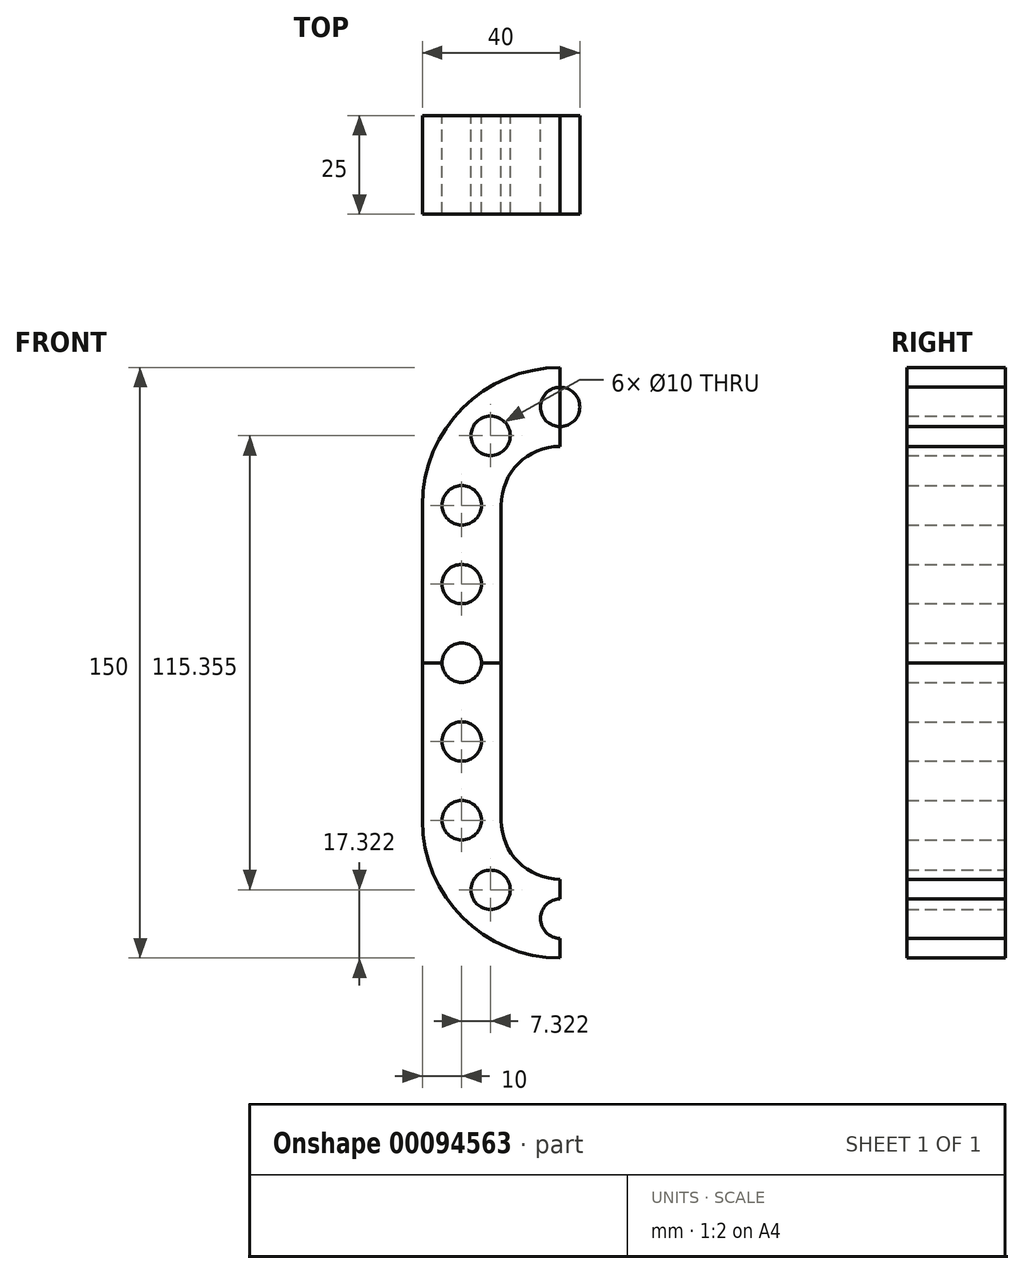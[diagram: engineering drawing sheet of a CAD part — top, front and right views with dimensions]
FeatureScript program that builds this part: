
annotation { "Feature Type Name" : "Feature", "Feature Type Description" : "" }
export const myFeature = defineFeature(function(context is Context, id is Id, definition is map)
    precondition{}
    {
        {
            var Q0;
            Q0=qCreatedBy(makeId("Front.planeOp"),FACE);
            var sketch = newSketch(context, id + "F0", { "sketchPlane" : qUnion([Q0])});
            skPoint(sketch, "E0", {"position": v(-25, 40) * mm});
            skLineSegment(sketch, "E1", {"start": v(-25, 40) * mm, "end": v(-25, 0) * mm, "construction": true});
            skArc(sketch, "E2", {"start": v(0, 65) * mm, "mid": v(-17.68, 57.68) * mm, "end": v(-25, 40) * mm, "construction": true});
            skLineSegment(sketch, "E3.0", {"start": v(-35, 40) * mm, "end": v(-35, 0) * mm});
            skArc(sketch, "E3.1", {"start": v(0, 75) * mm, "mid": v(-24.75, 64.75) * mm, "end": v(-35, 40) * mm});
            skLineSegment(sketch, "E4.0", {"start": v(-15, 40) * mm, "end": v(-15, 0) * mm});
            skArc(sketch, "E4.1", {"start": v(0, 55) * mm, "mid": v(-10.6, 50.6) * mm, "end": v(-15, 40) * mm});
            skArc(sketch, "E5.0.left", {"start": v(0, 55) * mm, "mid": v(-10.6, 50.6) * mm, "end": v(-15, 40) * mm, "construction": true});
            skArc(sketch, "E5.0.right", {"start": v(0, 75) * mm, "mid": v(-24.75, 64.75) * mm, "end": v(-35, 40) * mm, "construction": true});
            skLineSegment(sketch, "E5.1.startCap", {"start": v(-15, 40) * mm, "end": v(-15, 40) * mm});
            skLineSegment(sketch, "E5.1.left", {"start": v(-15, 40) * mm, "end": v(-15, 0) * mm, "construction": true});
            skLineSegment(sketch, "E5.1.right", {"start": v(-15, 40) * mm, "end": v(-15, 0) * mm, "construction": true});
            skCircle(sketch, "E6", {"center": v(-25, 40) * mm, "radius": 5 * mm});
            skArc(sketch, "E7.0.1.0", {"start": v(-25, 25) * mm, "mid": v(-30, 20) * mm, "end": v(-25, 15) * mm});
            skArc(sketch, "E7.0.2.0", {"start": v(-20, 0) * mm, "mid": v(-25, 5) * mm, "end": v(-30, 0) * mm});
            skLineSegment(sketch, "E7.direction1", {"start": v(-25, 40) * mm, "end": v(0, 40) * mm, "construction": true});
            skLineSegment(sketch, "E7.direction2", {"start": v(-25, 40) * mm, "end": v(-25, 20) * mm, "construction": true});
            skCircle(sketch, "E8.1.0", {"center": v(-17.68, 57.68) * mm, "radius": 5 * mm});
            skArc(sketch, "E8.2.0", {"start": v(0, 70) * mm, "mid": v(-5, 65) * mm, "end": v(0, 60) * mm});
            skLineSegment(sketch, "E8.anchor1", {"start": v(0, 40) * mm, "end": v(-25, 40) * mm, "construction": true});
            skLineSegment(sketch, "E8.anchor2", {"start": v(0, 40) * mm, "end": v(0, 65) * mm, "construction": true});
            skLineSegment(sketch, "E9", {"start": v(-15, 0) * mm, "end": v(-35, 0) * mm});
            skLineSegment(sketch, "E10", {"start": v(0, 75) * mm, "end": v(0, 55) * mm});
            skArc(sketch, "E11.MirrorCS", {"start": v(-25, 25) * mm, "mid": v(-20, 20) * mm, "end": v(-25, 15) * mm});
            skLineSegment(sketch, "E12.MirrorCS", {"start": v(15, 40) * mm, "end": v(15, 0) * mm, "construction": true});
            skArc(sketch, "E13.MirrorCS", {"start": v(0, 75) * mm, "mid": v(24.75, 64.75) * mm, "end": v(35, 40) * mm, "construction": true});
            skArc(sketch, "E14.MirrorCS", {"start": v(0, 55) * mm, "mid": v(10.6, 50.6) * mm, "end": v(15, 40) * mm, "construction": true});
            skLineSegment(sketch, "E15.MirrorCS", {"start": v(25, 40) * mm, "end": v(25, 20) * mm, "construction": true});
            skLineSegment(sketch, "E16.MirrorCS", {"start": v(25, 40) * mm, "end": v(0, 40) * mm, "construction": true});
            skArc(sketch, "E17.MirrorCS", {"start": v(25, 25) * mm, "mid": v(30, 20) * mm, "end": v(25, 15) * mm});
            skCircle(sketch, "E18.MirrorC", {"center": v(25, 40) * mm, "radius": 5 * mm});
            skArc(sketch, "E19.MirrorCS", {"start": v(0, 55) * mm, "mid": v(10.6, 50.6) * mm, "end": v(15, 40) * mm});
            skLineSegment(sketch, "E20.MirrorCS", {"start": v(15, 40) * mm, "end": v(15, 0) * mm});
            skArc(sketch, "E21.MirrorCS", {"start": v(0, 75) * mm, "mid": v(24.75, 64.75) * mm, "end": v(35, 40) * mm});
            skLineSegment(sketch, "E22.MirrorCS", {"start": v(35, 40) * mm, "end": v(35, 0) * mm});
            skLineSegment(sketch, "E23.MirrorCS", {"start": v(0, 40) * mm, "end": v(25, 40) * mm, "construction": true});
            skLineSegment(sketch, "E24.MirrorCS", {"start": v(25, 40) * mm, "end": v(25, 0) * mm, "construction": true});
            skCircle(sketch, "E25.MirrorC", {"center": v(17.68, 57.68) * mm, "radius": 5 * mm});
            skArc(sketch, "E26.MirrorCS", {"start": v(20, 0) * mm, "mid": v(25, 5) * mm, "end": v(30, 0) * mm});
            skArc(sketch, "E27.MirrorCS", {"start": v(25, 25) * mm, "mid": v(20, 20) * mm, "end": v(25, 15) * mm});
            skArc(sketch, "E28.MirrorCS", {"start": v(0, 70) * mm, "mid": v(5, 65) * mm, "end": v(0, 60) * mm});
            skLineSegment(sketch, "E29.MirrorCS", {"start": v(15, 0) * mm, "end": v(35, 0) * mm});
            skLineSegment(sketch, "E30.MirrorCS", {"start": v(15, 40) * mm, "end": v(15, 40) * mm});
            skArc(sketch, "E31.MirrorCS", {"start": v(0, 65) * mm, "mid": v(17.68, 57.68) * mm, "end": v(25, 40) * mm, "construction": true});
            skSolve(sketch);
        }
        {
            var Q0;
            {var subQ0=sQuery(id+"F0.wireOp",EDGE,"E3.0");Q0=makeQuery(id+"F0.imprint","IMPRINT",FACE,{"disambiguationData":[TD([[makeQuery(id+"F0.imprint","IMPRINT",EDGE,{"derivedFrom":subQ0}),1.0]])]});}
            var Q1;
            {var subQ0=sQuery(id+"F0.wireOp",EDGE,"E3.0");Q1=makeQuery(id+"F0.imprint","IMPRINT",FACE,{"disambiguationData":[TD([[makeQuery(id+"F0.imprint","IMPRINT",EDGE,{"derivedFrom":subQ0}),1.0]])]});}
            var Q2;
            Q2=makeQuery(id+"F0.imprint","IMPRINT",FACE,{"disambiguationData":[TD([[makeQuery(id+"F0.imprint","IMPRINT",EDGE,{"derivedFrom":sQuery(id+"F0.wireOp",EDGE,"E8.1.0")}),-1.0]])]});
            var Q3;
            {var subQ5=sQuery(id+"F0.wireOp",EDGE,"E28.MirrorCS");Q3=makeQuery(id+"F0.imprint","IMPRINT",FACE,{"disambiguationData":[TD([[makeQuery(id+"F0.imprint","IMPRINT",EDGE,{"derivedFrom":subQ5}),1.0]])]});}
            extrude(context, id + "F1", {"entities" : qUnion([Q0, Q1, Q2, Q3]), "depth" : 25 * mm});
        }
        {
            var Q0;
            Q0=makeQuery(id+"F1.opExtrude","SWEPT_BODY",BODY,{"disambiguationData":[OSD([sQuery(id+"F0.wireOp",EDGE,"E9"),sQuery(id+"F0.wireOp",EDGE,"E29.MirrorCS"),sQuery(id+"F0.wireOp",EDGE,"E28.MirrorCS"),sQuery(id+"F0.wireOp",EDGE,"E8.1.0"),sQuery(id+"F0.wireOp",EDGE,"E6"),sQuery(id+"F0.wireOp",EDGE,"E21.MirrorCS"),sQuery(id+"F0.wireOp",EDGE,"E7.0.1.0"),sQuery(id+"F0.wireOp",EDGE,"E20.MirrorCS"),sQuery(id+"F0.wireOp",EDGE,"E19.MirrorCS"),sQuery(id+"F0.wireOp",EDGE,"E18.MirrorC"),sQuery(id+"F0.wireOp",EDGE,"E17.MirrorCS"),sQuery(id+"F0.wireOp",EDGE,"E26.MirrorCS"),sQuery(id+"F0.wireOp",EDGE,"E3.1"),sQuery(id+"F0.wireOp",EDGE,"E8.2.0"),sQuery(id+"F0.wireOp",EDGE,"E4.0"),sQuery(id+"F0.wireOp",EDGE,"E4.1"),sQuery(id+"F0.wireOp",EDGE,"E3.0"),sQuery(id+"F0.wireOp",EDGE,"E25.MirrorC"),sQuery(id+"F0.wireOp",EDGE,"E11.MirrorCS"),sQuery(id+"F0.wireOp",EDGE,"E7.0.2.0"),sQuery(id+"F0.wireOp",EDGE,"E22.MirrorCS"),sQuery(id+"F0.wireOp",EDGE,"E27.MirrorCS")])]});
            var Q1;
            Q1=qCreatedBy(makeId("Top.planeOp"),FACE);
            mirror(context, id + "F2", {"operationType" : NewBodyOperationType.ADD, "entities" : qUnion([Q0]), "mirrorPlane" : qUnion([Q1])});
        }
    });
